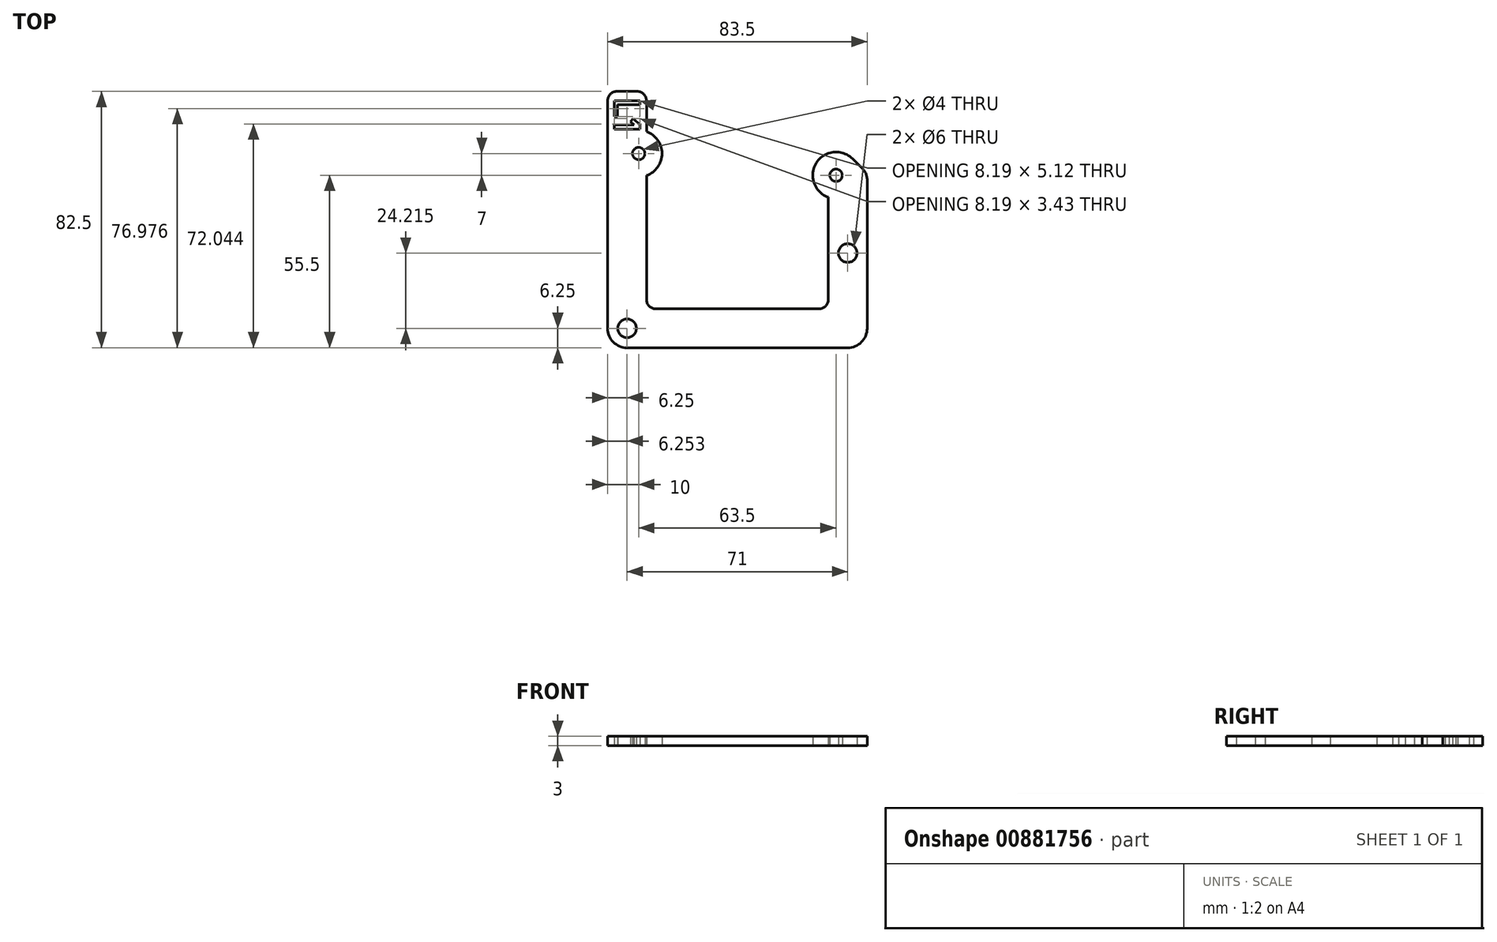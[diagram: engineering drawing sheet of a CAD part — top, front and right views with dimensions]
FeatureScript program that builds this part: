
annotation { "Feature Type Name" : "Feature", "Feature Type Description" : "" }
export const myFeature = defineFeature(function(context is Context, id is Id, definition is map)
    precondition{}
    {
        {
            var Q0;
            Q0=qCreatedBy(makeId("Top.planeOp"),FACE);
            var sketch = newSketch(context, id + "F0", { "sketchPlane" : qUnion([Q0])});
            skCircle(sketch, "E0", {"center": v(0, 0) * mm, "radius": 2 * mm});
            skCircle(sketch, "E1", {"center": v(-63.5, 7) * mm, "radius": 2 * mm});
            skLineSegment(sketch, "E2", {"start": v(-2.5, -7.07) * mm, "end": v(-2.5, -40) * mm});
            skLineSegment(sketch, "E3", {"start": v(-5.5, -43) * mm, "end": v(-58, -43) * mm});
            skLineSegment(sketch, "E4", {"start": v(-61, -40) * mm, "end": v(-61, -0.07) * mm});
            skLineSegment(sketch, "E5", {"start": v(-61, -0.07) * mm, "end": v(-61, -0.07) * mm});
            skLineSegment(sketch, "E6", {"start": v(-73.5, 24) * mm, "end": v(-73.5, -49.25) * mm});
            skLineSegment(sketch, "E7", {"start": v(-67.25, -55.5) * mm, "end": v(3.75, -55.5) * mm});
            skLineSegment(sketch, "E8", {"start": v(10, -49.25) * mm, "end": v(10, -1.46) * mm});
            skCircle(sketch, "E9", {"center": v(3.75, -25.04) * mm, "radius": 3 * mm});
            skCircle(sketch, "E10", {"center": v(-67.25, -49.25) * mm, "radius": 3 * mm});
            skArc(sketch, "E11", {"start": v(5.3, 5.3) * mm, "mid": v(-6.34, 4) * mm, "end": v(-2.5, -7.07) * mm});
            skLineSegment(sketch, "E12", {"start": v(8.54, 2.07) * mm, "end": v(5.3, 5.3) * mm});
            skLineSegment(sketch, "E13", {"start": v(-2.5, -25.04) * mm, "end": v(10, -25.04) * mm, "construction": true});
            skArc(sketch, "E14", {"start": v(-61, -0.07) * mm, "mid": v(-56, 7) * mm, "end": v(-61, 14.07) * mm});
            skLineSegment(sketch, "E15", {"start": v(-61, -43) * mm, "end": v(-73.5, -55.5) * mm, "construction": true});
            skPoint(sketch, "E16.visualSharp", {"position": v(-73.5, -55.5) * mm});
            skArc(sketch, "E16.filletArc", {"start": v(-73.5, -49.25) * mm, "mid": v(-71.67, -53.67) * mm, "end": v(-67.25, -55.5) * mm});
            skPoint(sketch, "E17.visualSharp", {"position": v(10, -55.5) * mm});
            skArc(sketch, "E17.filletArc", {"start": v(3.75, -55.5) * mm, "mid": v(8.17, -53.67) * mm, "end": v(10, -49.25) * mm});
            skPoint(sketch, "E18.visualSharp", {"position": v(10, 0.6) * mm});
            skArc(sketch, "E18.filletArc", {"start": v(10, -1.46) * mm, "mid": v(9.62, 0.45) * mm, "end": v(8.54, 2.07) * mm});
            skPoint(sketch, "E19.visualSharp", {"position": v(-61, -43) * mm});
            skArc(sketch, "E19.filletArc", {"start": v(-61, -40) * mm, "mid": v(-60.12, -42.12) * mm, "end": v(-58, -43) * mm});
            skPoint(sketch, "E20.visualSharp", {"position": v(-2.5, -43) * mm});
            skArc(sketch, "E20.filletArc", {"start": v(-5.5, -43) * mm, "mid": v(-3.38, -42.12) * mm, "end": v(-2.5, -40) * mm});
            skLineSegment(sketch, "E21", {"start": v(-61, 14.07) * mm, "end": v(-61, 24) * mm});
            skLineSegment(sketch, "E22", {"start": v(-64, 27) * mm, "end": v(-70.5, 27) * mm});
            skPoint(sketch, "E23.visualSharp", {"position": v(-61, 27) * mm});
            skArc(sketch, "E23.filletArc", {"start": v(-61, 24) * mm, "mid": v(-61.88, 26.12) * mm, "end": v(-64, 27) * mm});
            skPoint(sketch, "E24.visualSharp", {"position": v(-73.5, 27) * mm});
            skArc(sketch, "E24.filletArc", {"start": v(-70.5, 27) * mm, "mid": v(-72.62, 26.12) * mm, "end": v(-73.5, 24) * mm});
            skText(sketch, "E25", { "text": "L1", "fontName": "AllertaStencil-Regular.ttf"});
            skLineSegment(sketch, "E26", {"start": v(-70.5, 24) * mm, "end": v(-64, 24) * mm, "construction": true});
            skLineSegment(sketch, "E27", {"start": v(-67.25, 24) * mm, "end": v(-67.25, 19.57) * mm, "construction": true});
            const initialGuessF0  = {"E25": [-0.07134, 0.02507, 0, -1, 0.00819]};
            skSetInitialGuess(sketch, initialGuessF0);
            skSolve(sketch);
        }
        {
            var Q0;
            Q0 = qSketchRegion(id + "F0", true);
            extrude(context, id + "F1", {"entities" : qUnion([Q0]), "depth" : 3 * mm, "offsetDistance" : 25 * mm});
        }
    });
